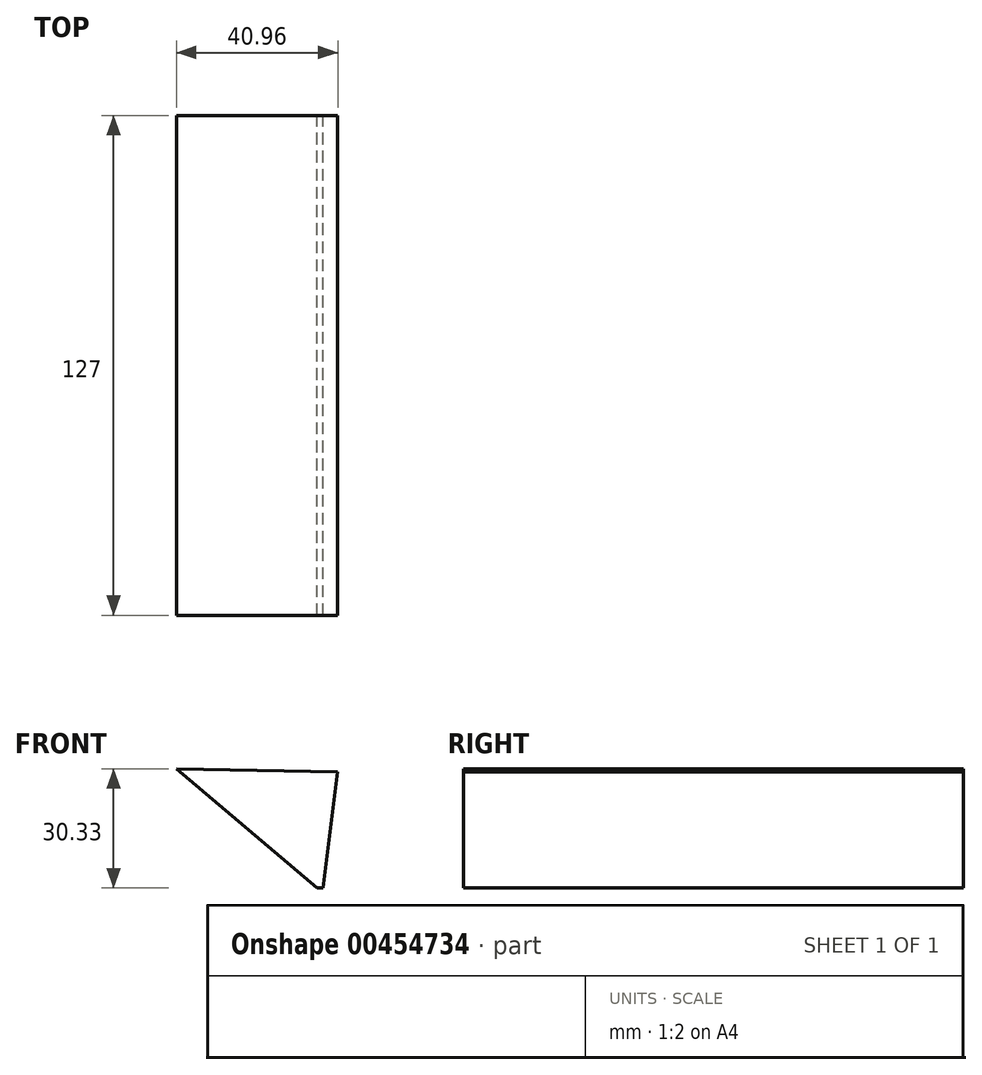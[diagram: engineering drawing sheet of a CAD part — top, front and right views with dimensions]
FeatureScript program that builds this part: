
annotation { "Feature Type Name" : "Feature", "Feature Type Description" : "" }
export const myFeature = defineFeature(function(context is Context, id is Id, definition is map)
    precondition{}
    {
        {
            var Q0;
            Q0=qCreatedBy(makeId("Front.planeOp"),FACE);
            var sketch = newSketch(context, id + "F0", { "sketchPlane" : qUnion([Q0])});
            skLineSegment(sketch, "E0", {"start": v(-67.3, 49.67) * mm, "end": v(-31.66, 19.34) * mm});
            skLineSegment(sketch, "E1", {"start": v(-26.35, 48.92) * mm, "end": v(-30.15, 19.34) * mm});
            skLineSegment(sketch, "E2", {"start": v(-67.3, 49.67) * mm, "end": v(-26.35, 48.92) * mm});
            skLineSegment(sketch, "E3", {"start": v(-30.15, 19.34) * mm, "end": v(-31.66, 19.34) * mm});
            skSolve(sketch);
        }
        {
            var Q0;
            Q0=makeQuery(id+"F0.imprint","IMPRINT",FACE,{"disambiguationData":[TD([[makeQuery(id+"F0.imprint","IMPRINT",EDGE,{"derivedFrom":sQuery(id+"F0.wireOp",EDGE,"E0")}),1.0]])]});
            extrude(context, id + "F1", {"entities" : qUnion([Q0]), "depth" : 127 * mm});
        }
    });
